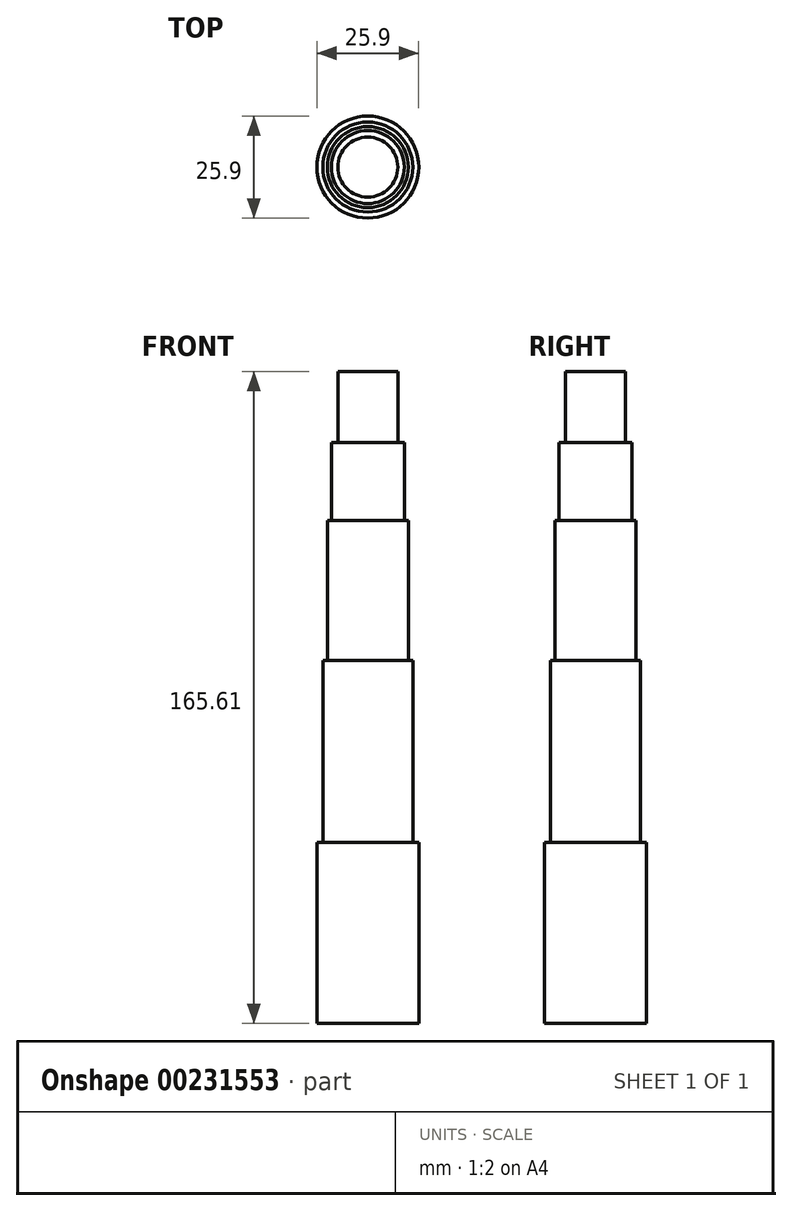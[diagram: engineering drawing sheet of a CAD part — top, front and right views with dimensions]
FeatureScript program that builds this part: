
annotation { "Feature Type Name" : "Feature", "Feature Type Description" : "" }
export const myFeature = defineFeature(function(context is Context, id is Id, definition is map)
    precondition{}
    {
        {
            var Q0;
            Q0=qCreatedBy(makeId("Top.planeOp"),FACE);
            var sketch = newSketch(context, id + "F0", { "sketchPlane" : qUnion([Q0])});
            skCircle(sketch, "E0", {"center": v(0, 0) * mm, "radius": 11.43 * mm});
            skCircle(sketch, "E1", {"center": v(0, 0) * mm, "radius": 10.29 * mm});
            skCircle(sketch, "E2", {"center": v(0, 0) * mm, "radius": 9.27 * mm});
            skCircle(sketch, "E3", {"center": v(0, 0) * mm, "radius": 12.95 * mm});
            skCircle(sketch, "E4", {"center": v(0, 0) * mm, "radius": 7.62 * mm});
            skSolve(sketch);
        }
        {
            var Q0;
            Q0=makeQuery(id+"F0.imprint","IMPRINT",FACE,{"disambiguationData":[TD([[makeQuery(id+"F0.imprint","IMPRINT",EDGE,{"derivedFrom":sQuery(id+"F0.wireOp",EDGE,"E0")}),-1.0]])]});
            extrude(context, id + "F1", {"entities" : qUnion([Q0]), "depth" : 45.97 * mm});
        }
        {
            var Q0;
            Q0=makeQuery(id+"F0.imprint","IMPRINT",FACE,{"disambiguationData":[TD([[makeQuery(id+"F0.imprint","IMPRINT",EDGE,{"derivedFrom":sQuery(id+"F0.wireOp",EDGE,"E0")}),1.0]])]});
            extrude(context, id + "F2", {"entities" : qUnion([Q0]), "operationType" : NewBodyOperationType.ADD, "depth" : 92.2 * mm});
        }
        {
            var Q0;
            Q0=makeQuery(id+"F0.imprint","IMPRINT",FACE,{"disambiguationData":[TD([[makeQuery(id+"F0.imprint","IMPRINT",EDGE,{"derivedFrom":sQuery(id+"F0.wireOp",EDGE,"E1")}),1.0]])]});
            extrude(context, id + "F3", {"entities" : qUnion([Q0]), "operationType" : NewBodyOperationType.ADD, "depth" : 127.76 * mm});
        }
        {
            var Q0;
            Q0=makeQuery(id+"F0.imprint","IMPRINT",FACE,{"disambiguationData":[TD([[makeQuery(id+"F0.imprint","IMPRINT",EDGE,{"derivedFrom":sQuery(id+"F0.wireOp",EDGE,"E2")}),1.0]])]});
            extrude(context, id + "F4", {"entities" : qUnion([Q0]), "operationType" : NewBodyOperationType.ADD, "depth" : 147.57 * mm});
        }
        {
            var Q0;
            Q0=makeQuery(id+"F0.imprint","IMPRINT",FACE,{"disambiguationData":[TD([[makeQuery(id+"F0.imprint","IMPRINT",EDGE,{"derivedFrom":sQuery(id+"F0.wireOp",EDGE,"E4")}),1.0]])]});
            extrude(context, id + "F5", {"entities" : qUnion([Q0]), "operationType" : NewBodyOperationType.ADD, "depth" : 165.6 * mm});
        }
    });
